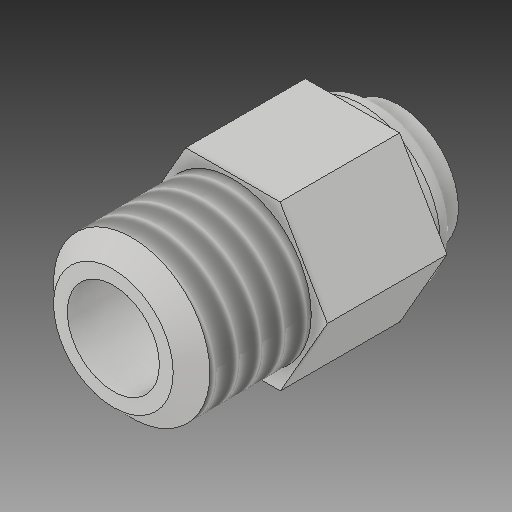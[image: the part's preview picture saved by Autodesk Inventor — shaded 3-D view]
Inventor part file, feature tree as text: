
AUTODESK INVENTOR PART (.ipt)
format: ipt  version: 2017 (Build 210142000, 142)  size: 174,080 bytes
history: native  units: mm
features: sketch x6, other x3
ambient origin geometry x8: Origin, YZ Plane, XZ Plane, XY Plane, X Axis, Y Axis, Z Axis, Center Point
bodies: Solid1 (feature_tree)
feature tree (9):
  other  "Pushfit-Adapter.ipt"
  other  "Solid1::Pushfit-Adapter.ipt"
  other  "TaggingFeature1"
  sketch  "Sketch1"  dims[d0=10.0mm]
  sketch  "Sketch2"
  sketch  "Sketch3"
  sketch  "Sketch4"
  sketch  "Sketch5"
  sketch  "Sketch6"
